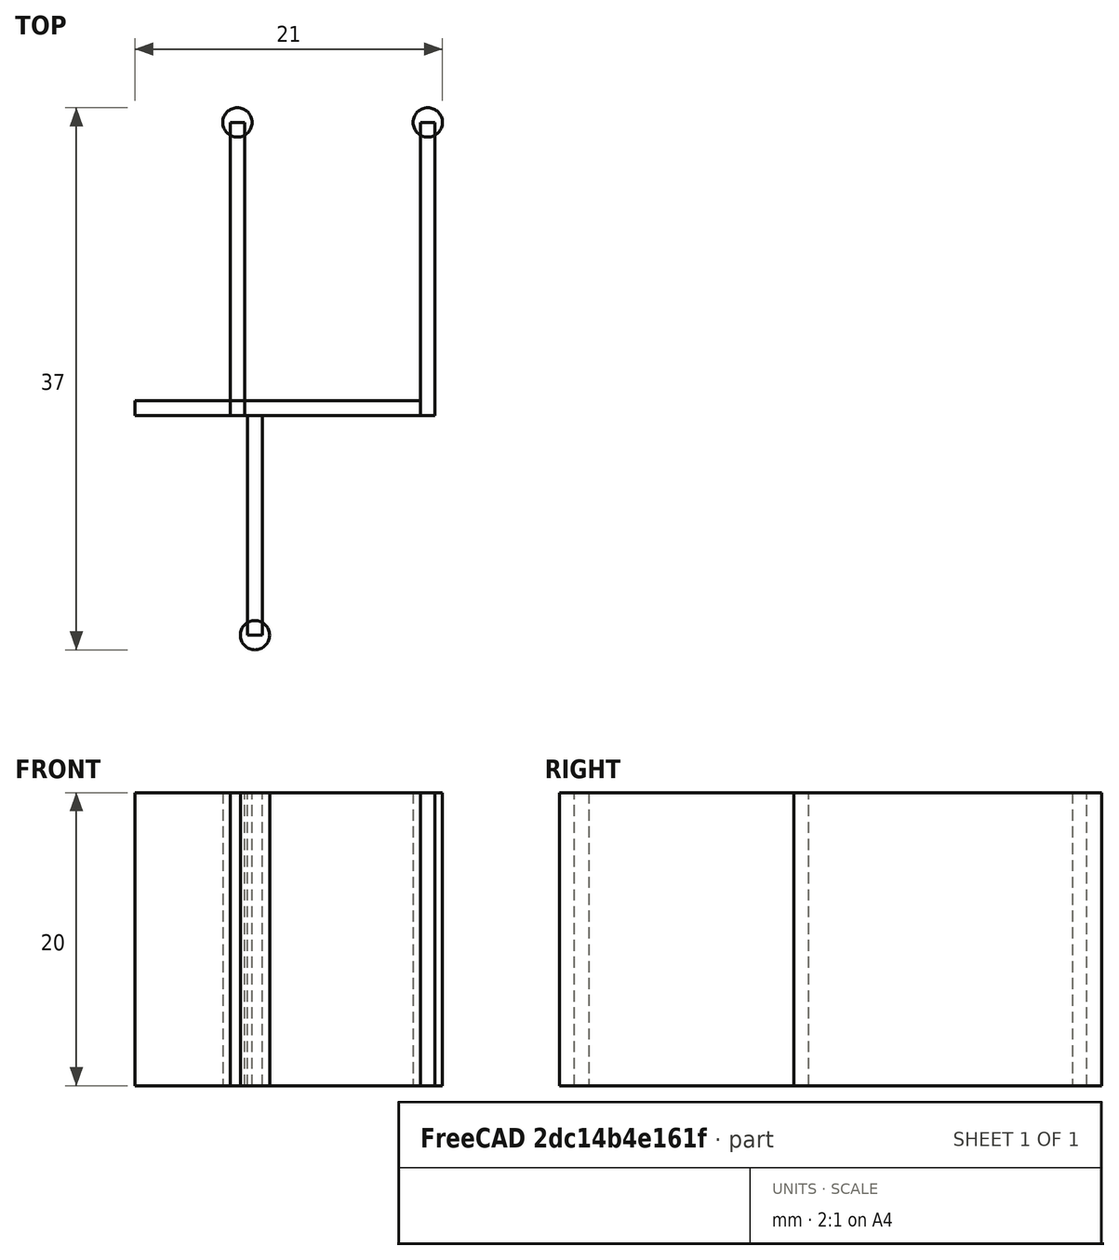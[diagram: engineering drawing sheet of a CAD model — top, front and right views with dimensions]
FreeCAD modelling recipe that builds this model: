
FCSTD DOCUMENT  (FreeCAD 1.0R39109 (Git))
Label: usb-holder-desk
License: All rights reserved
LicenseURL: http://en.wikipedia.org/wiki/All_rights_reserved
objects: Part::Box×4, Part::Cylinder×3, Sketcher::SketchObject×1
note: 9 computed .brp shape members not serialized (recipe doc carries the construction recipe); baked Part::Feature solids carry a one-line shape summary decoded from their .brp

FEATURE [Sketcher::SketchObject] Sketch
  ArcFitTolerance = 0
  FullyConstrained = true
  MakeInternals = false
FEATURE [Part::Box] Box  label="Cube"
  AttacherType = Attacher::AttachEngine3D
  Height = 20
  Length = 19.5
  Width = 1
FEATURE [Part::Box] Box001  label="Cube001"
  AttacherType = Attacher::AttachEngine3D
  Height = 20
  Length = 1
  Placement = pos=(6.5,0,0) rot=(0,0,1;0rad)
  Width = 20
FEATURE [Part::Box] Box002  label="Cube002"
  AttacherType = Attacher::AttachEngine3D
  Height = 20
  Length = 1
  Placement = pos=(19.5,0,0) rot=(0,0,1;0rad)
  Width = 20
FEATURE [Part::Cylinder] Cylinder
  Angle = 360
  AttacherType = Attacher::AttachEngine3D
  FirstAngle = 0
  Height = 20
  Placement = pos=(7,20,0) rot=(0,0,1;0rad)
  Radius = 1
  SecondAngle = 0
FEATURE [Part::Cylinder] Cylinder001
  Angle = 360
  AttacherType = Attacher::AttachEngine3D
  FirstAngle = 0
  Height = 20
  Placement = pos=(20,20,0) rot=(0,0,1;0rad)
  Radius = 1
  SecondAngle = 0
FEATURE [Part::Box] Box003  label="Cube003"
  AttacherType = Attacher::AttachEngine3D
  Height = 20
  Length = 1
  Placement = pos=(7.7,-15,0) rot=(0,0,1;0rad)
  Width = 15
FEATURE [Part::Cylinder] Cylinder002
  Angle = 360
  AttacherType = Attacher::AttachEngine3D
  FirstAngle = 0
  Height = 20
  Placement = pos=(8.2,-15,0) rot=(0,0,1;0rad)
  Radius = 1
  SecondAngle = 0
